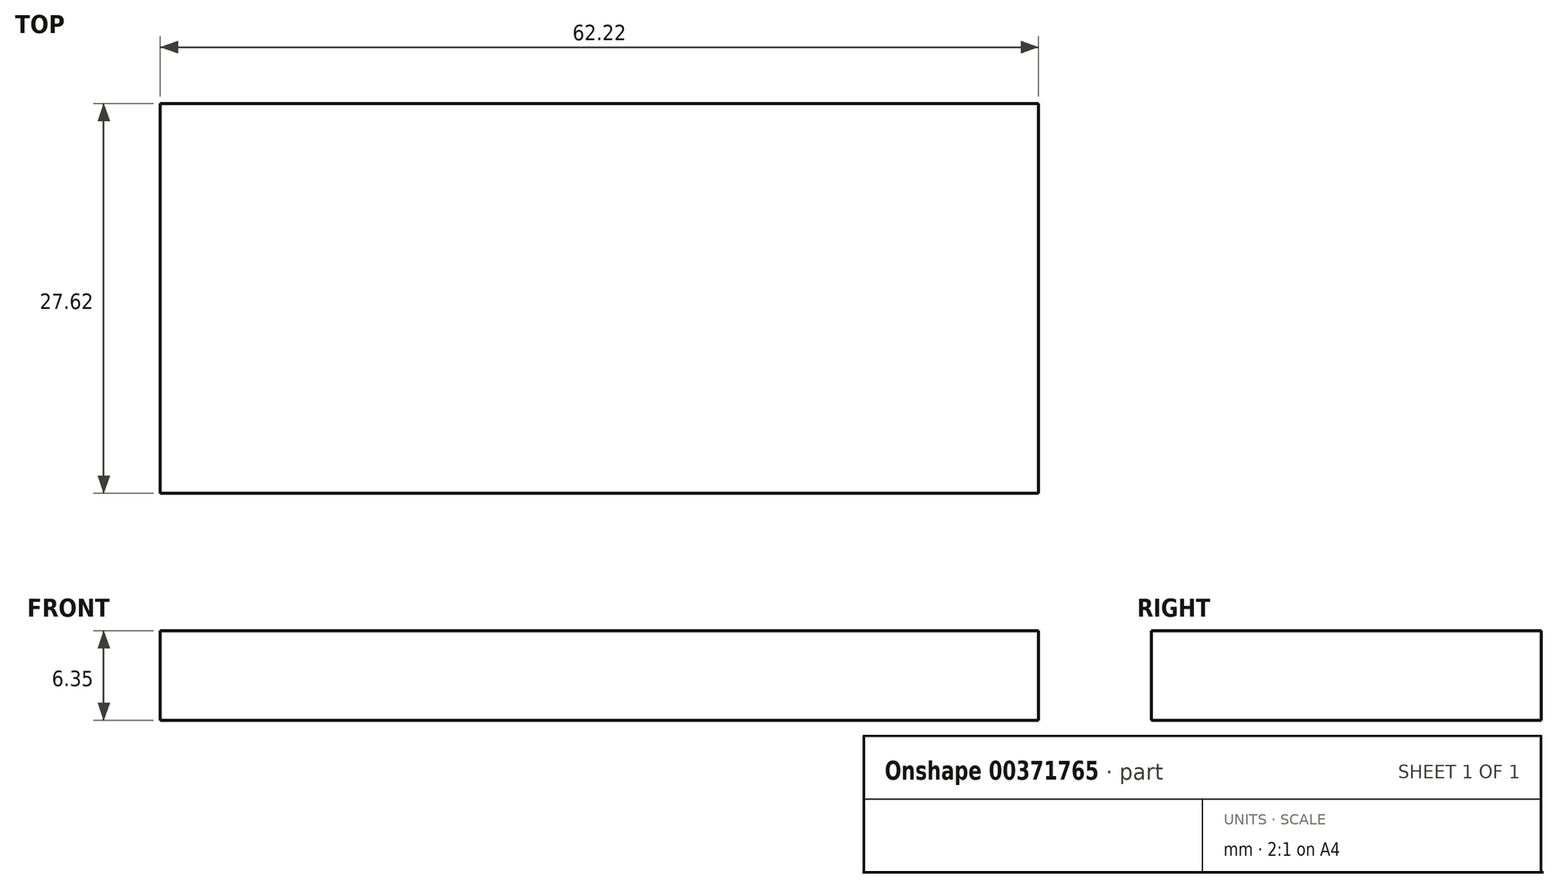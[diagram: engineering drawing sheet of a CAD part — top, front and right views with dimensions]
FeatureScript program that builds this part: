
annotation { "Feature Type Name" : "Feature", "Feature Type Description" : "" }
export const myFeature = defineFeature(function(context is Context, id is Id, definition is map)
    precondition{}
    {
        {
            var Q0;
            Q0=qCreatedBy(makeId("Top.planeOp"),FACE);
            var sketch = newSketch(context, id + "F0", { "sketchPlane" : qUnion([Q0])});
            skLineSegment(sketch, "E0.bottom", {"start": v(-35.98, 50.47) * mm, "end": v(26.24, 50.47) * mm});
            skLineSegment(sketch, "E0.top", {"start": v(-35.98, 22.85) * mm, "end": v(26.24, 22.85) * mm});
            skLineSegment(sketch, "E0.left", {"start": v(-35.98, 50.47) * mm, "end": v(-35.98, 22.85) * mm});
            skLineSegment(sketch, "E0.right", {"start": v(26.24, 50.47) * mm, "end": v(26.24, 22.85) * mm});
            skSolve(sketch);
        }
        {
            var Q0;
            Q0 = qSketchRegion(id + "F0", true);
            extrude(context, id + "F1", {"entities" : qUnion([Q0]), "depth" : 6.35 * mm});
        }
    });
